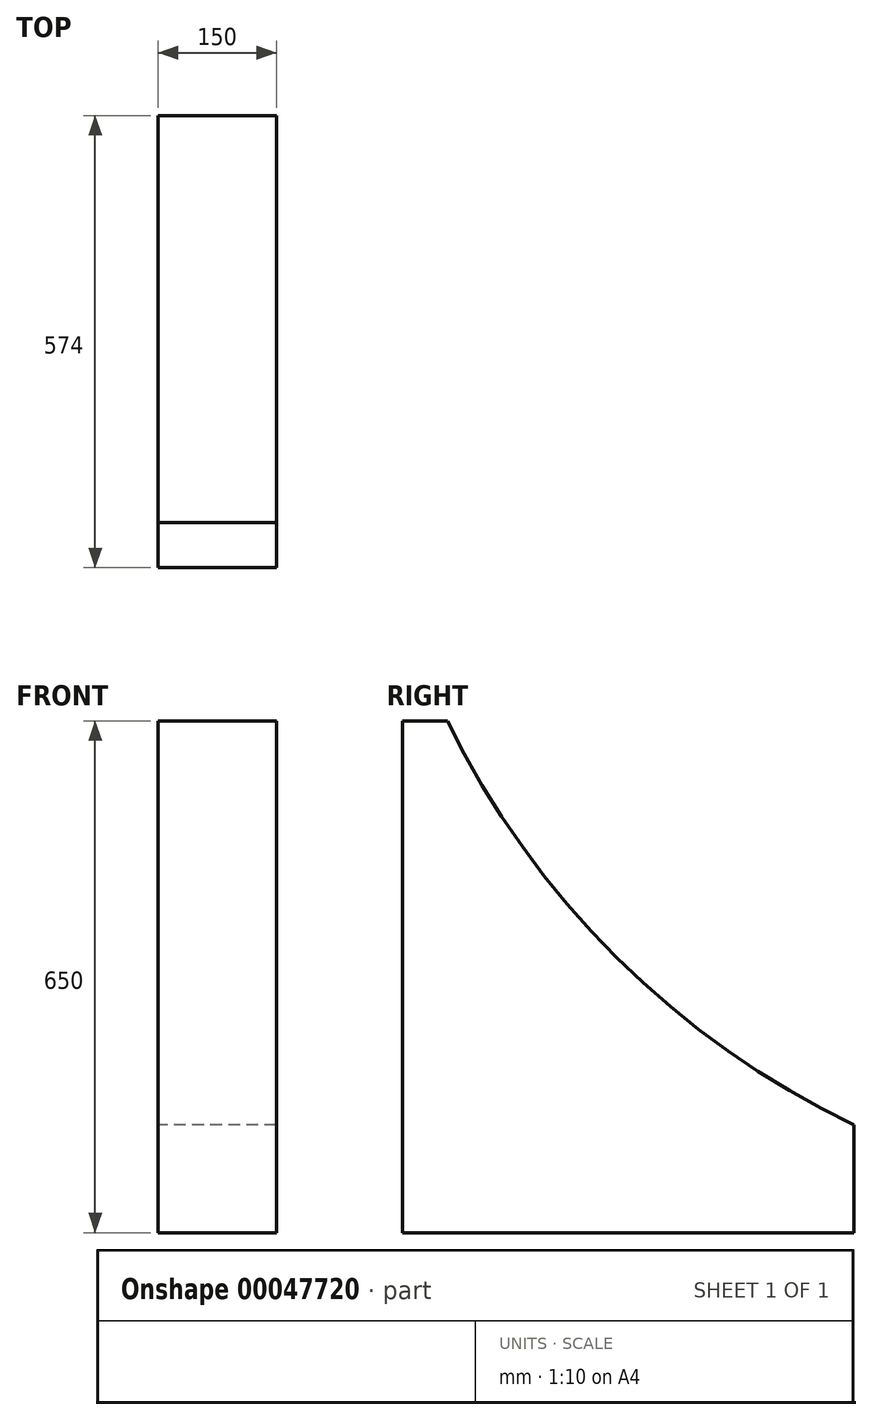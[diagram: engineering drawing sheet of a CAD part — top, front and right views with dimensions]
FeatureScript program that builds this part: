
annotation { "Feature Type Name" : "Feature", "Feature Type Description" : "" }
export const myFeature = defineFeature(function(context is Context, id is Id, definition is map)
    precondition{}
    {
        {
            var Q0;
            Q0=qCreatedBy(makeId("Right.planeOp"),FACE);
            var sketch = newSketch(context, id + "F0", { "sketchPlane" : qUnion([Q0])});
            skCircle(sketch, "E0", {"center": v(0, 0) * mm, "radius": 1100 * mm, "construction": true});
            skCircle(sketch, "E1", {"center": v(0, 0) * mm, "radius": 1108 * mm, "construction": true});
            skLineSegment(sketch, "E2", {"start": v(0, 0) * mm, "end": v(-1052.88, 0) * mm, "construction": true});
            skLineSegment(sketch, "E3", {"start": v(-1052.88, 0) * mm, "end": v(-1052.88, -486) * mm, "construction": true});
            skLineSegment(sketch, "E4", {"start": v(-1052.88, -486) * mm, "end": v(-1052.88, -1136) * mm});
            skLineSegment(sketch, "E5", {"start": v(-1052.88, -1136) * mm, "end": v(-478.88, -1136) * mm});
            skLineSegment(sketch, "E6", {"start": v(-478.88, -1136) * mm, "end": v(-478.88, -999.17) * mm});
            skLineSegment(sketch, "E7", {"start": v(-1052.88, -486) * mm, "end": v(-995.72, -486) * mm});
            skArc(sketch, "E8", {"start": v(-478.88, -999.17) * mm, "mid": v(-780.67, -786.26) * mm, "end": v(-995.72, -486) * mm});
            skSolve(sketch);
        }
        {
            var Q0;
            Q0 = qSketchRegion(id + "F0", true);
            extrude(context, id + "F1", {"entities" : qUnion([Q0]), "depth" : 150 * mm});
        }
    });
